# Revit family: ELiS C-W-200-bílá_RFA_2019
name_source: partatom
category: Mechanical Equipment
units: mm (PartAtom-declared; Revit-internal decimal feet)

## family parameters
Cut with Voids When Loaded = No
Host = Face
Part Type = Normal
Room Calculation Point = No
Round Connector Dimension = Use Diameter
Shared = No

## types (1)
- ELiS C-W-200
    Air flow = 0 m³/h
    Apparent power = 276 VA
    Connection = 3/4"
    Default Elevation = 2200 mm
    Description = Dveřní clona
    Fan = Single phase motor with diagonal rotor
    Heating capacity = 0 kW
    IP = 21
    Inlet air temperature (Tp1) = 0 °C
    Inlet water temperature (Tw1) = 0 °C
    Length = 2000 mm  [stored 6.56168 ft]
    Load classification = Motor
    Main Material = FLOWAIR-Steel-White
    Manufacturer = Hydronic Systems Prague s.r.o.
    Max. current consumption = 1 A
    Model = ELiS C-W-200
    Outlet air temperature (Tp2) = 0 °C
    Outlet water temperature (Tw2) = 0 °C
    Power ratio = 0.94
    Power supply voltage = 230 V
    Product data = 14289; bílá, délka 200cm, teplovodní; PN16; tmax=95°C
    Second Material = FLOWAIR-PerforatedSteel-White
    Type Comments = vnitřní instalace, neprašné prostředí; IP21; max dosah 3m na 3 rychlost
    URL = www.hydronic.cz
    Water pressure drop in the heat exchanger = 0 kPa
    Water stream flow in the heat exchanger = 0 L/s
    Weight of unit = 35.10 kg

note: [stored X ft] marks values corroborated as IEEE doubles in the binary element streams (Revit-internal decimal feet)
